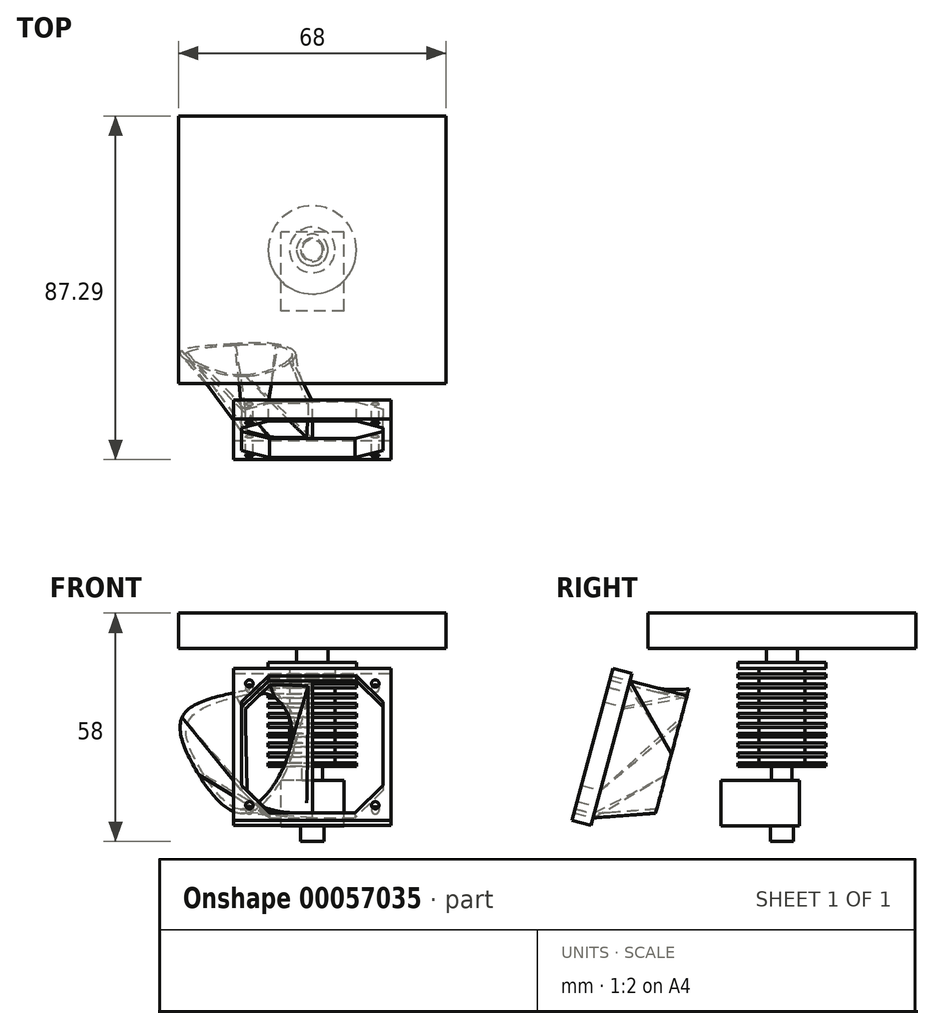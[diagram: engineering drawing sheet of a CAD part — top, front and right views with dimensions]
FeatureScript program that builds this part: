
annotation { "Feature Type Name" : "Feature", "Feature Type Description" : "" }
export const myFeature = defineFeature(function(context is Context, id is Id, definition is map)
    precondition{}
    {
        {
            var Q0;
            Q0=qCreatedBy(makeId("Top.planeOp"),FACE);
            var sketch = newSketch(context, id + "F0", { "sketchPlane" : qUnion([Q0])});
            skCircle(sketch, "E0", {"center": v(0, 0) * mm, "radius": 11.2 * mm});
            skSolve(sketch);
        }
        {
            var Q0;
            Q0 = qSketchRegion(id + "F0", true);
            extrude(context, id + "F1", {"entities" : qUnion([Q0]), "depth" : 30 * mm});
        }
        {
            var Q0;
            Q0=makeQuery(id+"F1.opExtrude","CAP_FACE",FACE,{"disambiguationData":[OSD([sQuery(id+"F0.wireOp",EDGE,"E0")])],"isStart":true});
            var sketch = newSketch(context, id + "F2", { "sketchPlane" : qUnion([Q0])});
            skCircle(sketch, "E1", {"center": v(0, 0) * mm, "radius": 2.61 * mm});
            skSolve(sketch);
        }
        {
            var Q0;
            Q0 = qSketchRegion(id + "F2", true);
            extrude(context, id + "F3", {"entities" : qUnion([Q0]), "operationType" : NewBodyOperationType.ADD, "depth" : 3.5 * mm});
        }
        {
            var Q0;
            Q0=makeQuery(id+"F3.opExtrude","CAP_FACE",FACE,{"disambiguationData":[OSD([sQuery(id+"F2.wireOp",EDGE,"E1")])],"isStart":false});
            var sketch = newSketch(context, id + "F4", { "sketchPlane" : qUnion([Q0])});
            skLineSegment(sketch, "E2.bottom", {"start": v(8, 15.5) * mm, "end": v(-8, 15.5) * mm});
            skLineSegment(sketch, "E2.top", {"start": v(8, -4.5) * mm, "end": v(-8, -4.5) * mm});
            skLineSegment(sketch, "E2.left", {"start": v(8, 15.5) * mm, "end": v(8, -4.5) * mm});
            skLineSegment(sketch, "E2.right", {"start": v(-8, 15.5) * mm, "end": v(-8, -4.5) * mm});
            skSolve(sketch);
        }
        {
            var Q0;
            Q0 = qSketchRegion(id + "F4", true);
            extrude(context, id + "F5", {"entities" : qUnion([Q0]), "operationType" : NewBodyOperationType.ADD, "depth" : 11.5 * mm});
        }
        {
            var Q0;
            Q0=makeQuery(id+"F5.opExtrude","CAP_FACE",FACE,{"disambiguationData":[OSD([sQuery(id+"F4.wireOp",EDGE,"E2.bottom"),sQuery(id+"F4.wireOp",EDGE,"E2.top"),sQuery(id+"F4.wireOp",EDGE,"E2.left"),sQuery(id+"F4.wireOp",EDGE,"E2.right")])],"isStart":false});
            var sketch = newSketch(context, id + "F6", { "sketchPlane" : qUnion([Q0])});
            skCircle(sketch, "E3", {"center": v(0, 0) * mm, "radius": 2.95 * mm});
            skSolve(sketch);
        }
        {
            var Q0;
            Q0 = qSketchRegion(id + "F6", true);
            extrude(context, id + "F7", {"entities" : qUnion([Q0]), "operationType" : NewBodyOperationType.ADD, "depth" : 4 * mm});
        }
        {
            var Q0;
            Q0=qCreatedBy(makeId("Right.planeOp"),FACE);
            var sketch = newSketch(context, id + "F8", { "sketchPlane" : qUnion([Q0])});
            skLineSegment(sketch, "E4", {"start": v(-13.4, 0) * mm, "end": v(-13.4, 35.84) * mm});
            skLineSegment(sketch, "E5", {"start": v(-13.4, 35.84) * mm, "end": v(-11.7, 35.84) * mm});
            skLineSegment(sketch, "E6", {"start": v(-11.7, 35.84) * mm, "end": v(-11.7, 35.31) * mm});
            skLineSegment(sketch, "E7", {"start": v(-13.4, 0) * mm, "end": v(-11.8, 0) * mm});
            skLineSegment(sketch, "E8", {"start": v(-11.8, 0) * mm, "end": v(-11.8, 1) * mm});
            skLineSegment(sketch, "E9", {"start": v(-11.8, 1) * mm, "end": v(-5.8, 1) * mm});
            skLineSegment(sketch, "E10", {"start": v(-5.8, 1) * mm, "end": v(-5.8, 2.5) * mm});
            skLineSegment(sketch, "E11", {"start": v(-5.8, 2.5) * mm, "end": v(-11.8, 2.5) * mm});
            skLineSegment(sketch, "E12", {"start": v(-5.8, 5) * mm, "end": v(-11.8, 5) * mm});
            skLineSegment(sketch, "E13", {"start": v(-5.8, 3.5) * mm, "end": v(-5.8, 5) * mm});
            skLineSegment(sketch, "E14", {"start": v(-11.8, 3.5) * mm, "end": v(-5.8, 3.5) * mm});
            skLineSegment(sketch, "E15", {"start": v(-11.8, 2.5) * mm, "end": v(-11.8, 3.5) * mm});
            skLineSegment(sketch, "E16", {"start": v(-5.8, 7.5) * mm, "end": v(-11.8, 7.5) * mm});
            skLineSegment(sketch, "E17", {"start": v(-5.8, 6) * mm, "end": v(-5.8, 7.5) * mm});
            skLineSegment(sketch, "E18", {"start": v(-11.8, 6) * mm, "end": v(-5.8, 6) * mm});
            skLineSegment(sketch, "E19", {"start": v(-11.8, 5) * mm, "end": v(-11.8, 6) * mm});
            skLineSegment(sketch, "E20", {"start": v(-5.8, 10) * mm, "end": v(-11.8, 10) * mm});
            skLineSegment(sketch, "E21", {"start": v(-5.8, 8.5) * mm, "end": v(-5.8, 10) * mm});
            skLineSegment(sketch, "E22", {"start": v(-11.8, 8.5) * mm, "end": v(-5.8, 8.5) * mm});
            skLineSegment(sketch, "E23", {"start": v(-11.8, 7.5) * mm, "end": v(-11.8, 8.5) * mm});
            skLineSegment(sketch, "E24", {"start": v(-5.8, 12.5) * mm, "end": v(-11.8, 12.5) * mm});
            skLineSegment(sketch, "E25", {"start": v(-5.8, 11) * mm, "end": v(-5.8, 12.5) * mm});
            skLineSegment(sketch, "E26", {"start": v(-11.8, 11) * mm, "end": v(-5.8, 11) * mm});
            skLineSegment(sketch, "E27", {"start": v(-11.8, 10) * mm, "end": v(-11.8, 11) * mm});
            skLineSegment(sketch, "E28", {"start": v(-11.8, 23.5) * mm, "end": v(-5.8, 23.5) * mm});
            skLineSegment(sketch, "E29", {"start": v(-11.8, 22.5) * mm, "end": v(-11.8, 23.5) * mm});
            skLineSegment(sketch, "E30", {"start": v(-11.8, 13.5) * mm, "end": v(-5.8, 13.5) * mm});
            skLineSegment(sketch, "E31", {"start": v(-5.8, 22.5) * mm, "end": v(-11.8, 22.5) * mm});
            skLineSegment(sketch, "E32", {"start": v(-5.8, 17.5) * mm, "end": v(-11.8, 17.5) * mm});
            skLineSegment(sketch, "E33", {"start": v(-5.8, 15) * mm, "end": v(-11.8, 15) * mm});
            skLineSegment(sketch, "E34", {"start": v(-5.8, 20) * mm, "end": v(-11.8, 20) * mm});
            skLineSegment(sketch, "E35", {"start": v(-11.8, 15) * mm, "end": v(-11.8, 16) * mm});
            skLineSegment(sketch, "E36", {"start": v(-11.8, 18.5) * mm, "end": v(-5.8, 18.5) * mm});
            skLineSegment(sketch, "E37", {"start": v(-5.8, 13.5) * mm, "end": v(-5.8, 15) * mm});
            skLineSegment(sketch, "E38", {"start": v(-11.8, 12.5) * mm, "end": v(-11.8, 13.5) * mm});
            skLineSegment(sketch, "E39", {"start": v(-11.8, 17.5) * mm, "end": v(-11.8, 18.5) * mm});
            skLineSegment(sketch, "E40", {"start": v(-5.8, 18.5) * mm, "end": v(-5.8, 20) * mm});
            skLineSegment(sketch, "E41", {"start": v(-11.8, 20) * mm, "end": v(-11.8, 21) * mm});
            skLineSegment(sketch, "E42", {"start": v(-5.8, 25) * mm, "end": v(-11.8, 25) * mm});
            skLineSegment(sketch, "E43", {"start": v(-5.8, 23.5) * mm, "end": v(-5.8, 25) * mm});
            skLineSegment(sketch, "E44", {"start": v(-5.8, 21) * mm, "end": v(-5.8, 22.5) * mm});
            skLineSegment(sketch, "E45", {"start": v(-11.8, 16) * mm, "end": v(-5.8, 16) * mm});
            skLineSegment(sketch, "E46", {"start": v(-11.8, 21) * mm, "end": v(-5.8, 21) * mm});
            skLineSegment(sketch, "E47", {"start": v(-5.8, 16) * mm, "end": v(-5.8, 17.5) * mm});
            skLineSegment(sketch, "E48", {"start": v(-11.7, 35.31) * mm, "end": v(-11.75, 30.5) * mm});
            skLineSegment(sketch, "E49", {"start": v(0, 37) * mm, "end": v(0, 0) * mm, "construction": true});
            skLineSegment(sketch, "E50", {"start": v(-11.79, 26.43) * mm, "end": v(-3.98, 26.35) * mm});
            skLineSegment(sketch, "E51", {"start": v(-3.98, 26.35) * mm, "end": v(-3.98, 30.43) * mm});
            skLineSegment(sketch, "E52", {"start": v(-3.98, 30.43) * mm, "end": v(-11.75, 30.5) * mm});
            skLineSegment(sketch, "E53.trimOffspring", {"start": v(-11.79, 26.43) * mm, "end": v(-11.8, 25) * mm});
            skSolve(sketch);
        }
        {
            var Q0;
            Q0=makeQuery(id+"F8.imprint","IMPRINT",FACE,{"disambiguationData":[TD([[makeQuery(id+"F8.imprint","IMPRINT",EDGE,{"derivedFrom":sQuery(id+"F8.wireOp",EDGE,"E4")}),-1.0]])]});
            var Q1;
            Q1=sQuery(id+"F8.wireOp",EDGE,"E49");
            revolve(context, id + "F9", {"operationType" : NewBodyOperationType.REMOVE, "entities" : qUnion([Q0]), "axis" : qUnion([Q1]), "revolveType" : RevolveType.FULL, "oppositeDirection" : true});
        }
        {
            var Q0;
            Q0=makeQuery(id+"F1.opExtrude","CAP_FACE",FACE,{"disambiguationData":[OSD([sQuery(id+"F0.wireOp",EDGE,"E0")])],"isStart":false});
            var sketch = newSketch(context, id + "F10", { "sketchPlane" : qUnion([Q0])});
            skLineSegment(sketch, "E54.bottom", {"start": v(34, 34) * mm, "end": v(-34, 34) * mm});
            skLineSegment(sketch, "E54.top", {"start": v(34, -34) * mm, "end": v(-34, -34) * mm});
            skLineSegment(sketch, "E54.left", {"start": v(34, 34) * mm, "end": v(34, -34) * mm});
            skLineSegment(sketch, "E54.right", {"start": v(-34, 34) * mm, "end": v(-34, -34) * mm});
            skSolve(sketch);
        }
        {
            var Q0;
            Q0 = qSketchRegion(id + "F10", true);
            extrude(context, id + "F11", {"entities" : qUnion([Q0]), "operationType" : NewBodyOperationType.ADD, "depth" : 9 * mm});
        }
        {
            var Q0;
            Q0=makeQuery(id+"F11.opExtrude","CAP_EDGE",EDGE,{"disambiguationData":[OSD([sQuery(id+"F10.wireOp",EDGE,"E54.top")])],"isStart":false});
            cPlane(context, id + "F12", {"entities" : qUnion([Q0]), "cplaneType" : CPlaneType.LINE_ANGLE, "offset" : 150 * mm, "angle" : 15 * degree, "width" : 150 * mm, "height" : 150 * mm});
        }
        {
            var Q0;
            Q0=qCreatedBy(id+"F12.planeOp",FACE);
            var sketch = newSketch(context, id + "F13", { "sketchPlane" : qUnion([Q0])});
            skLineSegment(sketch, "E55.bottom", {"start": v(-20, -26.98) * mm, "end": v(20, -26.98) * mm});
            skLineSegment(sketch, "E55.top", {"start": v(-20, 13.02) * mm, "end": v(0, 13.02) * mm});
            skLineSegment(sketch, "E55.left", {"start": v(-20, -26.98) * mm, "end": v(-20, 13.02) * mm});
            skLineSegment(sketch, "E55.right", {"start": v(20, -26.98) * mm, "end": v(20, 13.02) * mm});
            skLineSegment(sketch, "E56", {"start": v(0, 13.02) * mm, "end": v(20, 13.02) * mm});
            skLineSegment(sketch, "E57", {"start": v(0, 13.02) * mm, "end": v(0, -26.98) * mm, "construction": true});
            skPoint(sketch, "E58.centerSnap0", {"position": v(0, -6.98) * mm});
            skPoint(sketch, "E58.centerSnap1", {"position": v(-8.5, 13.02) * mm});
            skCircle(sketch, "E59", {"center": v(-16, 9.02) * mm, "radius": 0.95 * mm});
            skCircle(sketch, "E60.MirrorC", {"center": v(16, 9.02) * mm, "radius": 0.95 * mm});
            skPoint(sketch, "E61", {"position": v(0, -26.98) * mm});
            skLineSegment(sketch, "E62", {"start": v(-8.5, -6.98) * mm, "end": v(8.5, -6.98) * mm, "construction": true});
            skCircle(sketch, "E63.MirrorC", {"center": v(16, -22.98) * mm, "radius": 0.95 * mm});
            skCircle(sketch, "E64.MirrorC", {"center": v(-16, -22.98) * mm, "radius": 0.95 * mm});
            skLineSegment(sketch, "E65", {"start": v(-18, 4.19) * mm, "end": v(-18, -17.81) * mm});
            skLineSegment(sketch, "E66", {"start": v(-18, -17.81) * mm, "end": v(-10.83, -24.98) * mm});
            skLineSegment(sketch, "E67", {"start": v(-10.83, -24.98) * mm, "end": v(0, -24.98) * mm});
            skLineSegment(sketch, "E68", {"start": v(0, -24.98) * mm, "end": v(0, 11.02) * mm});
            skLineSegment(sketch, "E69", {"start": v(0, 11.02) * mm, "end": v(-11.17, 11.02) * mm});
            skLineSegment(sketch, "E70", {"start": v(-11.17, 11.02) * mm, "end": v(-18, 4.19) * mm});
            skLineSegment(sketch, "E71.MirrorCS", {"start": v(11.17, 11.02) * mm, "end": v(18, 4.19) * mm});
            skLineSegment(sketch, "E72.MirrorCS", {"start": v(0, 11.02) * mm, "end": v(11.17, 11.02) * mm});
            skLineSegment(sketch, "E73.MirrorCS", {"start": v(18, 4.19) * mm, "end": v(18, -17.81) * mm});
            skLineSegment(sketch, "E74.MirrorCS", {"start": v(18, -17.81) * mm, "end": v(10.83, -24.98) * mm});
            skLineSegment(sketch, "E75.MirrorCS", {"start": v(10.83, -24.98) * mm, "end": v(0, -24.98) * mm});
            skSolve(sketch);
        }
        {
            var Q0;
            Q0 = qSketchRegion(id + "F13", true);
            extrude(context, id + "F14", {"entities" : qUnion([Q0]), "depth" : 5 * mm});
        }
        {
            var Q0;
            Q0=makeQuery(id+"F5.opExtrude","CAP_EDGE",EDGE,{"disambiguationData":[OSD([sQuery(id+"F4.wireOp",EDGE,"E2.right")])],"isStart":true});
            cPlane(context, id + "F15", {"entities" : qUnion([Q0]), "cplaneType" : CPlaneType.LINE_ANGLE, "offset" : 150 * mm, "angle" : 115 * degree, "width" : 150 * mm, "height" : 150 * mm});
        }
        {
            var Q0;
            Q0=qCreatedBy(id+"F12.planeOp",FACE);
            cPlane(context, id + "F16", {"entities" : qUnion([Q0]), "cplaneType" : CPlaneType.OFFSET, "offset" : 15 * mm, "oppositeDirection" : true, "width" : 150 * mm, "height" : 150 * mm});
        }
        {
            var Q0;
            Q0=qCreatedBy(id+"F16.planeOp",FACE);
            var sketch = newSketch(context, id + "F17", { "sketchPlane" : qUnion([Q0])});
            skFitSpline(sketch, "E76", {"points": [v(-32.62, 6.32) * mm, v(-29.5, -8.5) * mm, v(-16.62, -19.63) * mm, v(-4.18, 1.37) * mm, v(-10.43, 12.32) * mm, v(-18.34, 12.24) * mm, v(-32.62, 6.32) * mm]});
            skSolve(sketch);
        }
        {
            var Q1;
            Q1=makeQuery(id+"F13.imprint","IMPRINT",FACE,{"disambiguationData":[TD([[makeQuery(id+"F13.imprint","IMPRINT",EDGE,{"derivedFrom":sQuery(id+"F13.wireOp",EDGE,"E65")}),1.0]])]});
            var Q2;
            Q2=makeQuery(id+"F17.imprint","IMPRINT",FACE,{"disambiguationData":[TD([[makeQuery(id+"F17.imprint","IMPRINT",EDGE,{"derivedFrom":sQuery(id+"F17.wireOp",EDGE,"E76")}),1.0]])]});
            loft(context, id + "F18", {"operationType" : NewBodyOperationType.ADD, "sheetProfilesArray" : [{ "sheetProfileEntities" : qUnion([Q1]) }, { "sheetProfileEntities" : qUnion([Q2]) }]});
        }
        {
            var Q0;
            Q0=makeQuery(id+"F18.opLoft","CAP_FACE",FACE,{"disambiguationData":[OSD([makeQuery(id+"F13.imprint","IMPRINT",FACE,{"disambiguationData":[TD([[makeQuery(id+"F13.imprint","IMPRINT",EDGE,{"derivedFrom":sQuery(id+"F13.wireOp",EDGE,"E65")}),1.0]])]})])],"isStart":true});
            var Q1;
            Q1=makeQuery(id+"F18.opLoft","CAP_FACE",FACE,{"disambiguationData":[OSD([makeQuery(id+"F17.imprint","IMPRINT",FACE,{"disambiguationData":[TD([[makeQuery(id+"F17.imprint","IMPRINT",EDGE,{"derivedFrom":sQuery(id+"F17.wireOp",EDGE,"E76")}),1.0]])]})])],"isStart":true});
            shell(context, id + "F19", {"entities" : qUnion([Q0, Q1]), "thickness" : 1 * mm});
        }
    });
